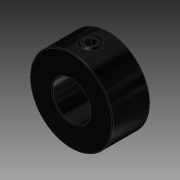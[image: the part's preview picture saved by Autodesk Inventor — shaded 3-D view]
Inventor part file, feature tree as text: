
AUTODESK INVENTOR PART (.ipt)
format: ipt  version: 2015 (Build 190159000, 159)  size: 162,304 bytes
history: native  units: in
note: dims shown in document units (in); Inventor stores cm internally (conversion verified against a paired STEP export)
features: other x2, imported_body x2, fillet x1
ambient origin geometry x8: Origin, YZ Plane, XZ Plane, XY Plane, X Axis, Y Axis, Z Axis, Center Point
bodies: Body1 (feature_tree), Body2 (feature_tree)
feature tree (5):
  fillet  "Fillet1"  [1 undecoded]
  other  "57485K6801"
  other  "Cut-Extrude2"
  imported_body  "Base1"
  imported_body  "Base2"
note: 1 required parameter value undecoded (feature->parameter linkage not recoverable at this tier; creation-order binding heuristic only, values carry confidence <= 0.55)
